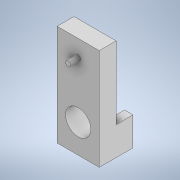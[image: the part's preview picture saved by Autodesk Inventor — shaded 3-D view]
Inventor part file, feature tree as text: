
AUTODESK INVENTOR PART (.ipt)
format: ipt  version: 2021 (Build 250183000, 183)  size: 129,024 bytes
history: native  units: mm
features: extrude x4, sketch x4, thread x1
ambient origin geometry x8: Origin, YZ Plane, XZ Plane, XY Plane, X Axis, Y Axis, Z Axis, Center Point
bodies: Solid1 (feature_tree)
feature tree (9):
  extrude  "Extrusion1"  Depth=25.0mm
  extrude  "Extrusion2"  Depth=10.0mm
  thread  "Thread1"  [1 undecoded]
  extrude  "Extrusion3"  Depth=6.0mm TaperAngle=0.0deg
  extrude  "Extrusion5"  Depth=10.0mm TaperAngle=0.0deg
  sketch  "Sketch1"  dims[d0=60.0mm d1=25.0mm]
  sketch  "Sketch2"  dims[d2=12.5mm d5=12.5mm d6=10.0mm d7=0.0mm]
  sketch  "Sketch3"  dims[d8=3.0mm d10=6.0mm d11=0.0mm]
  sketch  "Sketch5"  dims[d12=6.0mm d13=0.0mm d15=10.0mm d16=0.0mm d20=17.0mm d21=5.0mm d22=5.0mm d25=7.5mm d26=15.0mm d27=10.0mm d28=0.0mm d29=37.5mm d9=0.872665mm]
note: 1 required parameter value undecoded (feature->parameter linkage not recoverable at this tier; creation-order binding heuristic only, values carry confidence <= 0.55)
